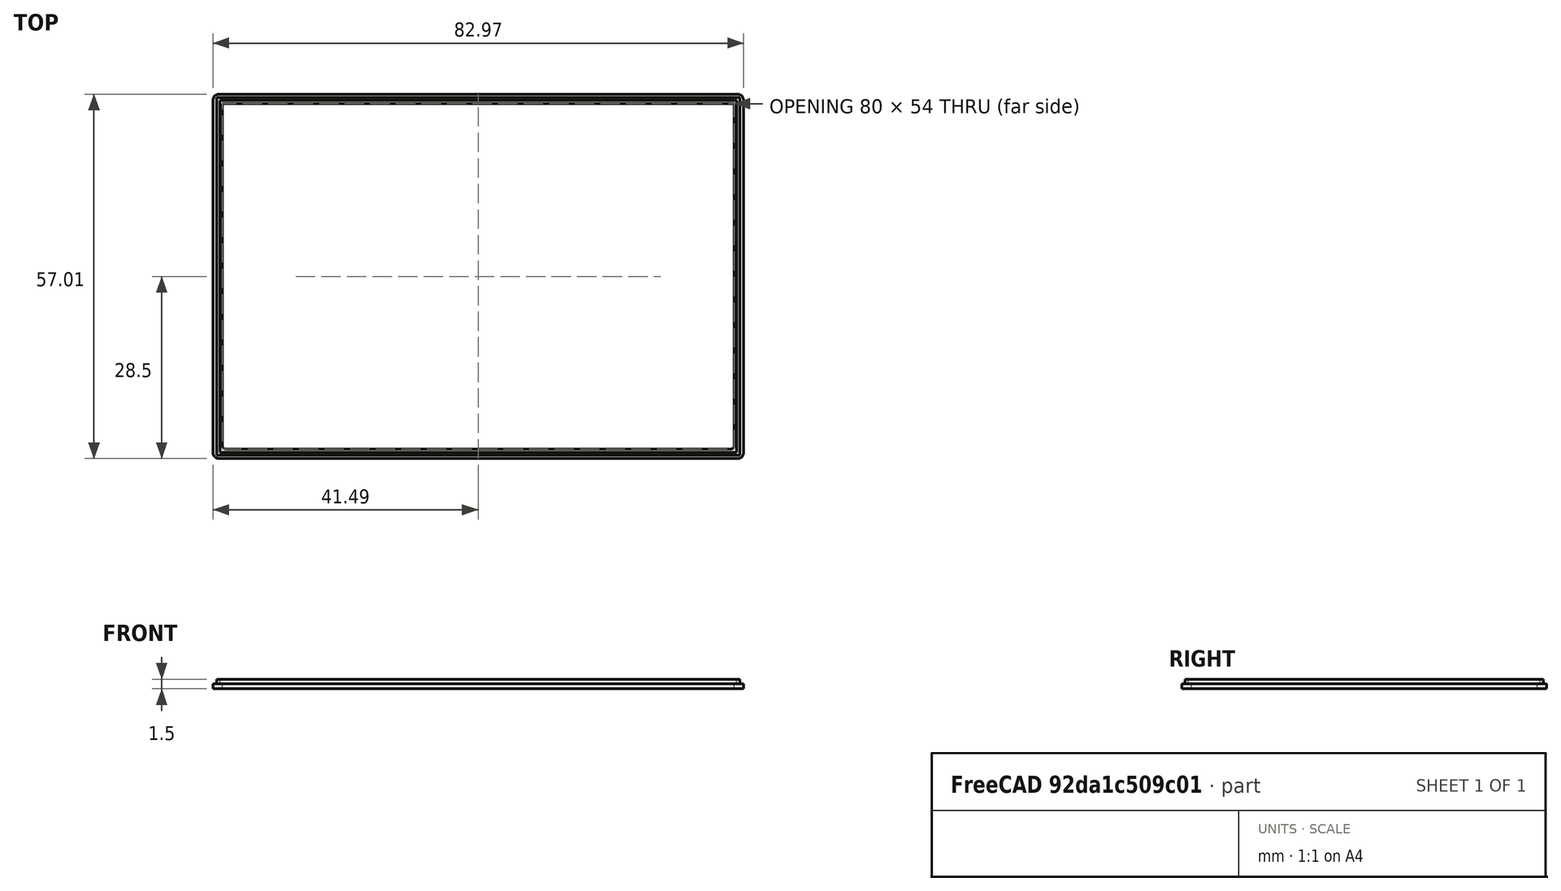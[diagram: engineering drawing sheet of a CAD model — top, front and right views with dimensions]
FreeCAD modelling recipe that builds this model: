
FCSTD DOCUMENT  (FreeCAD 0.18.4R)
Label: SmallBoxGasket3
License: All rights reserved
LicenseURL: http://en.wikipedia.org/wiki/All_rights_reserved
objects: Part::Box×3, Part::Cut×2, Sketcher::SketchObject×1, PartDesign::Pad×1, Part::Fillet×1, Part::MultiFuse×1, Mesh::Feature×1
note: 10 computed .brp shape members not serialized (recipe doc carries the construction recipe); baked Part::Feature solids carry a one-line shape summary decoded from their .brp

FEATURE [Sketcher::SketchObject] Sketch002
  MapMode = 5
  sketch-geometry (8):
    g0: LineSegment StartX=16.0115 StartY=-28 StartZ=0 EndX=-64.9999 EndY=-28 EndZ=0
    g1: LineSegment StartX=-65 StartY=29.005 StartZ=0 EndX=15.9984 EndY=29.005 EndZ=0
    g2: LineSegment StartX=16.9833 StartY=28.0201 StartZ=0 EndX=16.9833 EndY=-27.0282 EndZ=0
    g3: ArcOfCircle CenterX=16.0115 CenterY=-27.0282 CenterZ=0 NormalX=0 NormalY=0 NormalZ=1 AngleXU=0 Radius=0.97176 StartAngle=4.71239 EndAngle=6.28319
    g4: ArcOfCircle CenterX=15.9984 CenterY=28.0201 CenterZ=0 NormalX=0 NormalY=0 NormalZ=1 AngleXU=0 Radius=0.984903 StartAngle=1.051e-13 EndAngle=1.5708
    g5: LineSegment StartX=-65.9629 StartY=28.0426 StartZ=0 EndX=-65.987 EndY=-27.0125 EndZ=0
    g6: ArcOfCircle CenterX=-65 CenterY=28.0422 CenterZ=0 NormalX=0 NormalY=0 NormalZ=1 AngleXU=0 Radius=0.962855 StartAngle=1.5708 EndAngle=3.14115
    g7: ArcOfCircle CenterX=-64.9999 CenterY=-27.013 CenterZ=0 NormalX=0 NormalY=0 NormalZ=1 AngleXU=0 Radius=0.987031 StartAngle=3.14115 EndAngle=4.71239
  constraints (11):
    c: Horizontal(g0)
    c: Horizontal(g1)
    c: Vertical(g2)
    c: Tangent(g2,g3) = 1.5708
    c: Tangent(g0,g3) = 1.5708
    c: Tangent(g1,g4) = 1.5708
    c: Tangent(g2,g4) = 1.5708
    c: Tangent(g1,g6) = 1.5708
    c: Tangent(g5,g6) = -1.5708
    c: Tangent(g5,g7) = -1.5708
    c: Tangent(g0,g7) = 1.5708
FEATURE [PartDesign::Pad] Pad013
  Length = 0.75
  Length2 = 100
  Profile = -> Sketch002
  Type = 0
FEATURE [Part::Box] Box010  label="Würfel010"
  AttacherType = Attacher::AttachEngine3D
  Height = 3
  Length = 80
  Placement = pos=(-64.5,-26.5,-1) rot=(0,0,1;0rad)
  Width = 54
FEATURE [Part::Cut] Cut
  Base = -> Pad013
  Tool = -> Box010
FEATURE [Part::Fillet] Fillet
  Base = -> Cut
  Edges = 2 edges r=0.5: [Edge35,Edge36]
FEATURE [Part::Box] Box  label="Würfel"
  AttacherType = Attacher::AttachEngine3D
  Height = 1
  Length = 81.8
  Placement = pos=(-72.4,-27.5,1) rot=(0,0,1;0rad)
  Width = 56
FEATURE [Part::Box] Box011  label="Würfel011"
  AttacherType = Attacher::AttachEngine3D
  Height = 2
  Length = 80.8
  Placement = pos=(-71.9,-27,0.5) rot=(0,0,1;0rad)
  Width = 55
FEATURE [Part::Cut] Cut001
  Base = -> Box
  Placement = pos=(7,0,-0.5) rot=(0,0,1;0rad)
  Tool = -> Box011
FEATURE [Part::MultiFuse] Fusion
  Shapes = -> [Fillet,Cut001]
FEATURE [Mesh::Feature] Mesh  label="Fusion (Meshed)"
